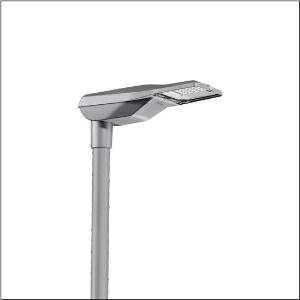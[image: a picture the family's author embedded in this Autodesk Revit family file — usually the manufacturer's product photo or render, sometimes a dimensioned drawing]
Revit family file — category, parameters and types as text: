
# Revit family: streetlight_sl_21_iq_micro___st1_0ab_5xe1m31d08db_7599
name_source: partatom
category: Lighting Fixtures
units: mm (PartAtom-declared; Revit-internal decimal feet)

## family parameters
Cut with Voids When Loaded = No
Host = Face
Light Source = No
Part Type = Normal
Room Calculation Point = No
Round Connector Dimension = Use Diameter
Shared = No

## types (1)
- --- (1 x LED, 4240 lm, 36.4 W, 3000K)
    Apparent Load = 36 VA
    CIE Flux Codes = 38 73 97 100 100
    Color Rendering = 70
    Color Temperature = 3000K
    Default Elevation = 1800 mm
    Description = Streetlight SL 21 iQ micro, mast luminaire, primary light control with lens, of PMMA, primary optical cover: cover, of toughened safety glass, transparent, light distribution: ST1.0aB, light emission: direct distribution, primary light characteristic: asymmetric, installation type: post-top, side-entry, LED, High Power LED, rated luminous flux: 4.240lm, luminous efficacy: 117lm/W, light colour: 730, colour temperature: 3000K, control: Auto-Match, Temp-Guard, Lumen-Switch, Night-Set, Smart-Wire, Light-Fading, Desk-Remote (wireless, voltage-free reading and setting of iQ features in the workshop via application-optimized NFC function/RFID function), optimised constant luminous flux control (CLO 2.0), pre-setting: linear dimming characteristic, mains connection: 220..240V, AC, 50/60Hz, start of lifetime: 36W, end of service life: 38W, reduction: 16W, luminaire housing, of diecast aluminium, powder-coated, Siteco® metallic grey (DB 702S), corrosivity category C5 mid according to DIN EN ISO 12944, please order mast flange separately, inclination adjustable: 0°, 5°, 10°, 15°, sealing non-destructively replaceable, multi-level sealing system, length: 528mm, width: 235mm, height: 110mm, mast flange for spigot size: 42mm (side-entry): 5XC10008XM4, 60/48mm (side-entry/post-top): 5XC10108XM2, 76/60mm (side-entry/post-top): 5XC10108XM1, protection rating (complete): IP66, insulation class (complete): insulation class II (safety insulation), certification: CE, ENEC, ENEC+, VDE, impact resistance: IK09, permissible operating ambient temperature for outdoor applications: -40..+50°C, standard-compliant lighting for roads and squares, packaging unit: 1 piece

Light Distribution: ST1.0aB
    Height = 110 mm
    Lamp = 1 x LED
    Lamp Light Flux = 4240 lm
    Lamp Power = 36.4 W
    Lamp count = 1
    Length = 528 mm
    Luminous efficacy = 116 lm/W
    Manufacturer = Siteco
    ModVariant = No
    Model = 5XE1M31D08DB
    Number of Poles = 1
    OnlyDefault = Yes
    Power Factor = 1
    Product Name = Streetlight SL 21 iQ micro | ST1.0aB
    Product group = mast luminaire | pylon top
    ProductGroupID = 6100
    Protection Class = Protection class II
    Protection Degree = IP 66
    RLX_Detail_Level = 1
    RLX_Emergency_Light_Flux = 0 lm
    RLX_Emergency_Type = 0
    RLX_Emergency_Type_DB = No
    RlxData = <blob elided: 98969 chars, md5=f7ab33ed>
    Socket = socket
    Standby Power = 0 W
    System Light Flux = 4240 lm
    System Power = 36 W
    Type Comments = factory setting: luminous flux: 100 % | dim-lin: 254 | 715 mA
    Type Image = l_1006881.jpg
    URL = http://relux.com
    VarID = @adj_124463
    Voltage = 0 V
    Weight = 0.00 kg
    Width = 235 mm

## geometry (parser evidence)
native form markers: Blend x4, Sweep x9
no freeform markers — native parametric forms only
